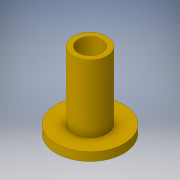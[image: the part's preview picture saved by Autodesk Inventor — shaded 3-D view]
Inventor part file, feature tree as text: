
AUTODESK INVENTOR PART (.ipt)
format: ipt  version: 2016 (Build 200138000, 138)  size: 109,568 bytes
history: native  units: in
note: dims shown in document units (in); Inventor stores cm internally (conversion verified against a paired STEP export)
features: extrude x4, sketch x4
ambient origin geometry x8: Origin, YZ Plane, XZ Plane, XY Plane, X Axis, Y Axis, Z Axis, Center Point
bodies: Solid1 (feature_tree)
feature tree (8):
  extrude  "Extrusion1"  Depth=1.0in TaperAngle=0.0deg
  extrude  "Extrusion2"  Depth=1.125in TaperAngle=0.0deg
  extrude  "Extrusion3"  Depth=0.125in TaperAngle=0.0deg
  extrude  "Extrusion4"  Depth=0.125in TaperAngle=0.0deg
  sketch  "Sketch1"  dims[d0=0.5in d1=1.0in d2=0.0in]
  sketch  "Sketch2"  dims[d3=0.35in d4=1.125in d5=0.0in]
  sketch  "Sketch3"  dims[d6=1.0in d7=0.125in d8=0.0in]
  sketch  "Sketch4"  dims[d9=0.35in d10=0.125in d11=0.0in]
